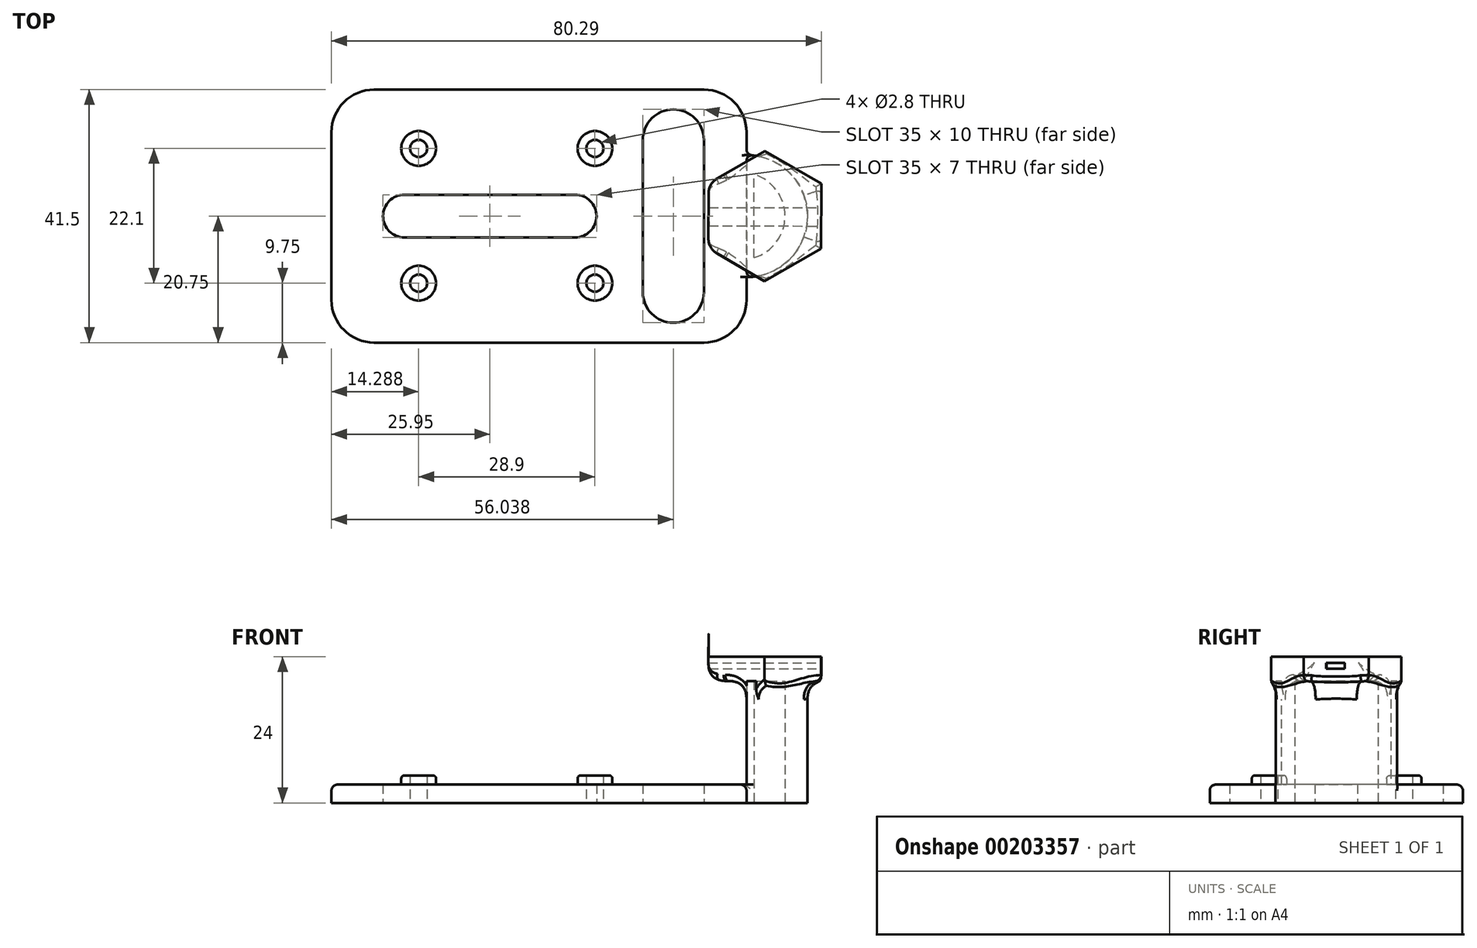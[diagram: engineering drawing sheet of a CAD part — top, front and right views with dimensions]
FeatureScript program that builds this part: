
annotation { "Feature Type Name" : "Feature", "Feature Type Description" : "" }
export const myFeature = defineFeature(function(context is Context, id is Id, definition is map)
    precondition{}
    {
        {
            var Q0;
            Q0=qCreatedBy(makeId("Top.planeOp"),FACE);
            var sketch = newSketch(context, id + "F0", { "sketchPlane" : qUnion([Q0])});
            skLineSegment(sketch, "E0.bottom", {"start": v(42.09, 20.75) * mm, "end": v(-25.95, 20.75) * mm});
            skLineSegment(sketch, "E0.top", {"start": v(42.09, -20.75) * mm, "end": v(-25.95, -20.75) * mm});
            skLineSegment(sketch, "E0.left", {"start": v(42.09, 20.75) * mm, "end": v(42.09, -20.75) * mm});
            skPoint(sketch, "E0.middle", {"position": v(0, 0) * mm});
            skCircle(sketch, "E1", {"center": v(-11.66, 11.1) * mm, "radius": 2.85 * mm});
            skCircle(sketch, "E2", {"center": v(-11.66, -11) * mm, "radius": 2.85 * mm});
            skCircle(sketch, "E3", {"center": v(17.24, 11.1) * mm, "radius": 2.85 * mm});
            skCircle(sketch, "E4", {"center": v(17.24, -11) * mm, "radius": 2.85 * mm});
            skCircle(sketch, "E5", {"center": v(-11.66, 11.1) * mm, "radius": 1.4 * mm});
            skCircle(sketch, "E6", {"center": v(17.24, 11.1) * mm, "radius": 1.4 * mm});
            skCircle(sketch, "E7", {"center": v(-11.66, -11) * mm, "radius": 1.4 * mm});
            skCircle(sketch, "E8", {"center": v(17.24, -11) * mm, "radius": 1.4 * mm});
            skLineSegment(sketch, "E9.left", {"start": v(-25.95, 12.5) * mm, "end": v(-25.95, -12.5) * mm});
            skLineSegment(sketch, "E10.bottom", {"start": v(14, 3.5) * mm, "end": v(-14, 3.5) * mm});
            skLineSegment(sketch, "E10.top", {"start": v(14, -3.5) * mm, "end": v(-14, -3.5) * mm});
            skLineSegment(sketch, "E10.left", {"start": v(17.5, 0) * mm, "end": v(17.5, 0) * mm});
            skLineSegment(sketch, "E10.right", {"start": v(-17.5, 0) * mm, "end": v(-17.5, 0) * mm});
            skLineSegment(sketch, "E11.bottom", {"start": v(30.09, 17.5) * mm, "end": v(30.09, 17.5) * mm});
            skLineSegment(sketch, "E11.top", {"start": v(30.09, -17.5) * mm, "end": v(30.09, -17.5) * mm});
            skLineSegment(sketch, "E11.left", {"start": v(35.09, 12.5) * mm, "end": v(35.09, -12.5) * mm});
            skLineSegment(sketch, "E11.right", {"start": v(25.09, 12.5) * mm, "end": v(25.09, -12.5) * mm});
            skPoint(sketch, "E11.middle", {"position": v(30.09, 0) * mm});
            skPoint(sketch, "E12.visualSharp", {"position": v(-25.95, 17.5) * mm});
            skPoint(sketch, "E13.visualSharp", {"position": v(-25.95, -17.5) * mm});
            skPoint(sketch, "E14.visualSharp", {"position": v(25.09, -17.5) * mm});
            skArc(sketch, "E14.filletArc", {"start": v(25.09, -12.5) * mm, "mid": v(26.55, -16.04) * mm, "end": v(30.09, -17.5) * mm});
            skPoint(sketch, "E15.visualSharp", {"position": v(35.09, -17.5) * mm});
            skArc(sketch, "E15.filletArc", {"start": v(30.09, -17.5) * mm, "mid": v(33.62, -16.04) * mm, "end": v(35.09, -12.5) * mm});
            skPoint(sketch, "E16.visualSharp", {"position": v(35.09, 17.5) * mm});
            skArc(sketch, "E16.filletArc", {"start": v(35.09, 12.5) * mm, "mid": v(33.62, 16.04) * mm, "end": v(30.09, 17.5) * mm});
            skPoint(sketch, "E17.visualSharp", {"position": v(25.09, 17.5) * mm});
            skArc(sketch, "E17.filletArc", {"start": v(30.09, 17.5) * mm, "mid": v(26.55, 16.04) * mm, "end": v(25.09, 12.5) * mm});
            skPoint(sketch, "E18.visualSharp", {"position": v(17.5, 3.5) * mm});
            skArc(sketch, "E18.filletArc", {"start": v(17.5, 0) * mm, "mid": v(16.47, 2.47) * mm, "end": v(14, 3.5) * mm});
            skPoint(sketch, "E19.visualSharp", {"position": v(17.5, -3.5) * mm});
            skArc(sketch, "E19.filletArc", {"start": v(14, -3.5) * mm, "mid": v(16.47, -2.47) * mm, "end": v(17.5, 0) * mm});
            skPoint(sketch, "E20.visualSharp", {"position": v(-17.5, -3.5) * mm});
            skArc(sketch, "E20.filletArc", {"start": v(-17.5, 0) * mm, "mid": v(-16.47, -2.47) * mm, "end": v(-14, -3.5) * mm});
            skPoint(sketch, "E21.visualSharp", {"position": v(-17.5, 3.5) * mm});
            skArc(sketch, "E21.filletArc", {"start": v(-14, 3.5) * mm, "mid": v(-16.47, 2.47) * mm, "end": v(-17.5, 0) * mm});
            skArc(sketch, "E22", {"start": v(42.09, -10) * mm, "mid": v(52.09, 0) * mm, "end": v(42.09, 10) * mm});
            skArc(sketch, "E23", {"start": v(43.34, -6.83) * mm, "mid": v(48.4, 0) * mm, "end": v(43.34, 6.83) * mm});
            skLineSegment(sketch, "E24", {"start": v(43.34, -6.83) * mm, "end": v(43.34, 6.83) * mm});
            skLineSegment(sketch, "E25", {"start": v(-25.95, 20.75) * mm, "end": v(-25.95, -20.75) * mm});
            skSolve(sketch);
        }
        {
            var Q0;
            Q0=makeQuery(id+"F0.imprint","IMPRINT",FACE,{"disambiguationData":[TD([[makeQuery(id+"F0.imprint","IMPRINT",EDGE,{"derivedFrom":sQuery(id+"F0.wireOp",EDGE,"E0.bottom")}),1.0]])]});
            var Q1;
            Q1=makeQuery(id+"F0.imprint","IMPRINT",FACE,{"disambiguationData":[TD([[makeQuery(id+"F0.imprint","IMPRINT",EDGE,{"derivedFrom":sQuery(id+"F0.wireOp",EDGE,"E3")}),1.0]])]});
            var Q2;
            Q2=makeQuery(id+"F0.imprint","IMPRINT",FACE,{"disambiguationData":[TD([[makeQuery(id+"F0.imprint","IMPRINT",EDGE,{"derivedFrom":sQuery(id+"F0.wireOp",EDGE,"E1")}),1.0]])]});
            var Q3;
            Q3=makeQuery(id+"F0.imprint","IMPRINT",FACE,{"disambiguationData":[TD([[makeQuery(id+"F0.imprint","IMPRINT",EDGE,{"derivedFrom":sQuery(id+"F0.wireOp",EDGE,"E2")}),1.0]])]});
            var Q4;
            Q4=makeQuery(id+"F0.imprint","IMPRINT",FACE,{"disambiguationData":[TD([[makeQuery(id+"F0.imprint","IMPRINT",EDGE,{"derivedFrom":sQuery(id+"F0.wireOp",EDGE,"E4")}),1.0]])]});
            extrude(context, id + "F1", {"entities" : qUnion([Q0, Q1, Q2, Q3, Q4]), "depth" : 3 * mm});
        }
        {
            var Q0;
            Q0=makeQuery(id+"F0.imprint","IMPRINT",FACE,{"disambiguationData":[TD([[makeQuery(id+"F0.imprint","IMPRINT",EDGE,{"derivedFrom":sQuery(id+"F0.wireOp",EDGE,"E1")}),1.0]])]});
            var Q1;
            Q1=makeQuery(id+"F0.imprint","IMPRINT",FACE,{"disambiguationData":[TD([[makeQuery(id+"F0.imprint","IMPRINT",EDGE,{"derivedFrom":sQuery(id+"F0.wireOp",EDGE,"E2")}),1.0]])]});
            var Q2;
            Q2=makeQuery(id+"F0.imprint","IMPRINT",FACE,{"disambiguationData":[TD([[makeQuery(id+"F0.imprint","IMPRINT",EDGE,{"derivedFrom":sQuery(id+"F0.wireOp",EDGE,"E4")}),1.0]])]});
            var Q3;
            Q3=makeQuery(id+"F0.imprint","IMPRINT",FACE,{"disambiguationData":[TD([[makeQuery(id+"F0.imprint","IMPRINT",EDGE,{"derivedFrom":sQuery(id+"F0.wireOp",EDGE,"E3")}),1.0]])]});
            extrude(context, id + "F2", {"entities" : qUnion([Q0, Q1, Q2, Q3]), "operationType" : NewBodyOperationType.ADD, "depth" : 4.5 * mm});
        }
        {
            var Q0;
            Q0=makeQuery(id+"F1.opExtrude","SWEPT_EDGE",EDGE,{"disambiguationData":[OSD([sQuery(id+"F0.wireOp",EDGE,"E0.top"),sQuery(id+"F0.wireOp",EDGE,"E0.right")])]});
            var Q1;
            Q1=makeQuery(id+"F1.opExtrude","SWEPT_EDGE",EDGE,{"disambiguationData":[OSD([sQuery(id+"F0.wireOp",EDGE,"E0.bottom"),sQuery(id+"F0.wireOp",EDGE,"E0.right")])]});
            var Q2;
            Q2=makeQuery(id+"F1.opExtrude","SWEPT_EDGE",EDGE,{"disambiguationData":[OSD([sQuery(id+"F0.wireOp",EDGE,"E0.top"),sQuery(id+"F0.wireOp",EDGE,"E0.left")])]});
            var Q3;
            Q3=makeQuery(id+"F1.opExtrude","SWEPT_EDGE",EDGE,{"disambiguationData":[OSD([sQuery(id+"F0.wireOp",EDGE,"E0.bottom"),sQuery(id+"F0.wireOp",EDGE,"E0.left")])]});
            fillet(context, id + "F3", {"entities" : qUnion([Q0, Q1, Q2, Q3]), "radius" : 7 * mm, "tangentPropagation" : true, "allowEdgeOverflow" : false});
        }
        {
            var Q0;
            Q0=makeQuery(id+"F2.opExtrude","CAP_EDGE",EDGE,{"disambiguationData":[OSD([sQuery(id+"F0.wireOp",EDGE,"E3")])],"isStart":false});
            var Q1;
            Q1=makeQuery(id+"F2.opExtrude","CAP_EDGE",EDGE,{"disambiguationData":[OSD([sQuery(id+"F0.wireOp",EDGE,"E1")])],"isStart":false});
            var Q2;
            Q2=makeQuery(id+"F2.opExtrude","CAP_EDGE",EDGE,{"disambiguationData":[OSD([sQuery(id+"F0.wireOp",EDGE,"E2")])],"isStart":false});
            var Q3;
            Q3=makeQuery(id+"F2.opExtrude","CAP_EDGE",EDGE,{"disambiguationData":[OSD([sQuery(id+"F0.wireOp",EDGE,"E4")])],"isStart":false});
            fillet(context, id + "F4", {"entities" : qUnion([Q0, Q1, Q2, Q3]), "radius" : 0.5 * mm, "tangentPropagation" : true, "allowEdgeOverflow" : false});
        }
        {
            var Q0;
            {var subQ0=sQuery(id+"F0.wireOp",EDGE,"E22");Q0=makeQuery(id+"F0.imprint","IMPRINT",FACE,{"disambiguationData":[TD([[makeQuery(id+"F0.imprint","IMPRINT",EDGE,{"derivedFrom":subQ0}),1.0]])]});}
            extrude(context, id + "F5", {"entities" : qUnion([Q0]), "operationType" : NewBodyOperationType.ADD, "depth" : 20 * mm});
        }
        {
            var Q0;
            Q0=makeQuery(id+"F5.opExtrude","CAP_FACE",FACE,{"disambiguationData":[OSD([sQuery(id+"F0.wireOp",EDGE,"E0.left"),sQuery(id+"F0.wireOp",EDGE,"E22"),sQuery(id+"F0.wireOp",EDGE,"E23"),sQuery(id+"F0.wireOp",EDGE,"E24")])],"isStart":false});
            var sketch = newSketch(context, id + "F6", { "sketchPlane" : qUnion([Q0])});
            skCircle(sketch, "E26.cCircle", {"center": v(45.08, 0) * mm, "radius": 9.24 * mm, "construction": true});
            skLineSegment(sketch, "E26.0", {"start": v(45.11, 10.67) * mm, "end": v(54.34, 5.31) * mm});
            skLineSegment(sketch, "E26.1", {"start": v(54.34, 5.31) * mm, "end": v(54.3, -5.36) * mm});
            skLineSegment(sketch, "E26.2", {"start": v(54.3, -5.36) * mm, "end": v(45.05, -10.67) * mm});
            skLineSegment(sketch, "E26.3", {"start": v(45.05, -10.67) * mm, "end": v(35.83, -5.31) * mm});
            skLineSegment(sketch, "E26.4", {"start": v(35.83, -5.31) * mm, "end": v(35.86, 5.36) * mm});
            skLineSegment(sketch, "E26.5", {"start": v(35.86, 5.36) * mm, "end": v(45.11, 10.67) * mm});
            skPoint(sketch, "E26.0.midPoint", {"position": v(49.72, 7.99) * mm});
            skSolve(sketch);
        }
        {
            var Q0;
            Q0 = qSketchRegion(id + "F6", true);
            extrude(context, id + "F7", {"entities" : qUnion([Q0]), "operationType" : NewBodyOperationType.ADD, "depth" : 4 * mm});
        }
        {
            var Q0;
            {var subQ0=sQuery(id+"F0.wireOp",EDGE,"E0.left");var subQ1=sQuery(id+"F0.wireOp",EDGE,"E22");Q0=makeQuery(id+"F5.boolean.opBoolean","SPLIT",EDGE,{"disambiguationData":[topologyDisambiguationEdgeConnected([makeQuery(id+"F5.opExtrude","SWEPT_FACE",FACE,{"disambiguationData":[OSD([subQ0])]})])],"derivedFrom":makeQuery(id+"F5.opExtrude","SWEPT_EDGE",EDGE,{"disambiguationData":[OSD([subQ0,subQ1]),TDD([makeQuery(id+"F0.imprint","INTERSECT",VERTEX,{"disambiguationData":[OD(0.0)],"derivedFrom":[subQ0,subQ1]})])]})});}
            var Q1;
            {var subQ0=sQuery(id+"F0.wireOp",EDGE,"E0.left");var subQ1=sQuery(id+"F0.wireOp",EDGE,"E22");Q1=makeQuery(id+"F5.boolean.opBoolean","SPLIT",EDGE,{"disambiguationData":[topologyDisambiguationEdgeConnected([makeQuery(id+"F5.opExtrude","SWEPT_FACE",FACE,{"disambiguationData":[OSD([subQ0])]})])],"derivedFrom":makeQuery(id+"F5.opExtrude","SWEPT_EDGE",EDGE,{"disambiguationData":[OSD([subQ0,subQ1]),TDD([makeQuery(id+"F0.imprint","INTERSECT",VERTEX,{"disambiguationData":[OD(1.0)],"derivedFrom":[subQ0,subQ1]})])]})});}
            fillet(context, id + "F8", {"entities" : qUnion([Q0, Q1]), "radius" : 1 * mm, "tangentPropagation" : true, "rho" : 0.5, "crossSection" : FilletCrossSection.CONIC, "allowEdgeOverflow" : false});
        }
        {
            var Q0;
            {var subQ0=sQuery(id+"F0.wireOp",EDGE,"E0.left");var subQ1=sQuery(id+"F0.wireOp",EDGE,"E22");Q0=makeQuery(id+"F5.boolean.opBoolean","SPLIT",EDGE,{"disambiguationData":[topologyDisambiguationEdgeConnected([makeQuery(id+"F1.opExtrude","SWEPT_FACE",FACE,{"disambiguationData":[OSD([subQ0])]})])],"derivedFrom":makeQuery(id+"F5.opExtrude","SWEPT_EDGE",EDGE,{"disambiguationData":[OSD([subQ0,subQ1]),TDD([makeQuery(id+"F0.imprint","INTERSECT",VERTEX,{"disambiguationData":[OD(1.0)],"derivedFrom":[subQ0,subQ1]})])]})});}
            var Q1;
            {var subQ0=sQuery(id+"F0.wireOp",EDGE,"E0.left");var subQ1=sQuery(id+"F0.wireOp",EDGE,"E22");Q1=makeQuery(id+"F5.boolean.opBoolean","SPLIT",EDGE,{"disambiguationData":[topologyDisambiguationEdgeConnected([makeQuery(id+"F1.opExtrude","SWEPT_FACE",FACE,{"disambiguationData":[OSD([subQ0])]})])],"derivedFrom":makeQuery(id+"F5.opExtrude","SWEPT_EDGE",EDGE,{"disambiguationData":[OSD([subQ0,subQ1]),TDD([makeQuery(id+"F0.imprint","INTERSECT",VERTEX,{"disambiguationData":[OD(0.0)],"derivedFrom":[subQ0,subQ1]})])]})});}
            fillet(context, id + "F9", {"entities" : qUnion([Q0, Q1]), "radius" : 1 * mm, "tangentPropagation" : true, "allowEdgeOverflow" : false});
        }
        {
            var Q0;
            {var subQ0=sQuery(id+"F0.wireOp",EDGE,"E0.left");Q0=makeQuery(id+"F7.boolean.opBoolean","SPLIT",EDGE,{"disambiguationData":[topologyDisambiguationEdgeConnected([makeQuery(id+"F5.opExtrude","SWEPT_FACE",FACE,{"disambiguationData":[OSD([subQ0])]}),makeQuery(id+"F7.opExtrude","CAP_FACE",FACE,{"disambiguationData":[OSD([sQuery(id+"F6.wireOp",EDGE,"E26.0"),sQuery(id+"F6.wireOp",EDGE,"E26.1"),sQuery(id+"F6.wireOp",EDGE,"E26.2"),sQuery(id+"F6.wireOp",EDGE,"E26.3"),sQuery(id+"F6.wireOp",EDGE,"E26.4"),sQuery(id+"F6.wireOp",EDGE,"E26.5")])],"isStart":true})])],"derivedFrom":makeQuery(id+"F5.opExtrude","CAP_EDGE",EDGE,{"disambiguationData":[OSD([subQ0])],"isStart":false})});}
            var Q1;
            Q1=makeQuery(id+"F7.opExtrude","CAP_EDGE",EDGE,{"disambiguationData":[OSD([sQuery(id+"F6.wireOp",EDGE,"E26.4")])],"isStart":true});
            var Q2;
            {var subQ0=sQuery(id+"F0.wireOp",EDGE,"E22");Q2=makeQuery(id+"F7.boolean.opBoolean","SPLIT",EDGE,{"disambiguationData":[topologyDisambiguationEdgeConnected([makeQuery(id+"F5.opExtrude","SWEPT_FACE",FACE,{"disambiguationData":[OSD([subQ0])]}),makeQuery(id+"F7.opExtrude","CAP_FACE",FACE,{"disambiguationData":[OSD([sQuery(id+"F6.wireOp",EDGE,"E26.0"),sQuery(id+"F6.wireOp",EDGE,"E26.1"),sQuery(id+"F6.wireOp",EDGE,"E26.2"),sQuery(id+"F6.wireOp",EDGE,"E26.3"),sQuery(id+"F6.wireOp",EDGE,"E26.4"),sQuery(id+"F6.wireOp",EDGE,"E26.5")])],"isStart":true})])],"derivedFrom":makeQuery(id+"F5.opExtrude","CAP_EDGE",EDGE,{"disambiguationData":[OSD([subQ0])],"isStart":false})});}
            var Q3;
            Q3=makeQuery(id+"F7.opExtrude","SWEPT_EDGE",EDGE,{"disambiguationData":[OSD([sQuery(id+"F6.wireOp",EDGE,"E26.3"),sQuery(id+"F6.wireOp",EDGE,"E26.4")])]});
            var Q4;
            Q4=makeQuery(id+"F7.opExtrude","SWEPT_EDGE",EDGE,{"disambiguationData":[OSD([sQuery(id+"F6.wireOp",EDGE,"E26.4"),sQuery(id+"F6.wireOp",EDGE,"E26.5")])]});
            fillet(context, id + "F10", {"entities" : qUnion([Q0, Q1, Q2, Q3, Q4]), "radius" : 3 * mm, "tangentPropagation" : true, "rho" : 0.5, "crossSection" : FilletCrossSection.CONIC, "allowEdgeOverflow" : false});
        }
        {
            var Q0;
            {var subQ0=sQuery(id+"F0.wireOp",EDGE,"E0.left");Q0=makeQuery(id+"F5.boolean.opBoolean","SPLIT",EDGE,{"disambiguationData":[topologyDisambiguationEdgeConnected([makeQuery(id+"F1.opExtrude","CAP_FACE",FACE,{"disambiguationData":[OSD([sQuery(id+"F0.wireOp",EDGE,"E0.bottom"),sQuery(id+"F0.wireOp",EDGE,"E0.top"),subQ0,sQuery(id+"F0.wireOp",EDGE,"E5"),sQuery(id+"F0.wireOp",EDGE,"E6"),sQuery(id+"F0.wireOp",EDGE,"E7"),sQuery(id+"F0.wireOp",EDGE,"E8"),sQuery(id+"F0.wireOp",EDGE,"E10.bottom"),sQuery(id+"F0.wireOp",EDGE,"E10.top"),sQuery(id+"F0.wireOp",EDGE,"E11.left"),sQuery(id+"F0.wireOp",EDGE,"E11.right"),sQuery(id+"F0.wireOp",EDGE,"E14.filletArc"),sQuery(id+"F0.wireOp",EDGE,"E15.filletArc"),sQuery(id+"F0.wireOp",EDGE,"E16.filletArc"),sQuery(id+"F0.wireOp",EDGE,"E17.filletArc"),sQuery(id+"F0.wireOp",EDGE,"E18.filletArc"),sQuery(id+"F0.wireOp",EDGE,"E19.filletArc"),sQuery(id+"F0.wireOp",EDGE,"E20.filletArc"),sQuery(id+"F0.wireOp",EDGE,"E21.filletArc"),sQuery(id+"F0.wireOp",EDGE,"E25")])],"isStart":false}),makeQuery(id+"F5.opExtrude","SWEPT_FACE",FACE,{"disambiguationData":[OSD([subQ0])]})])],"derivedFrom":makeQuery(id+"F1.opExtrude","CAP_EDGE",EDGE,{"disambiguationData":[OSD([subQ0])],"isStart":false})});}
            var Q1;
            {var subQ0=sQuery(id+"F6.wireOp",EDGE,"E26.3");var subQ1=sQuery(id+"F0.wireOp",EDGE,"E0.left");Q1=makeQuery(id+"F10.opFillet","BLEND_EDGE",EDGE,{"blendedFrom":[makeQuery(id+"F7.boolean.opBoolean","SPLIT",EDGE,{"disambiguationData":[topologyDisambiguationEdgeConnected([makeQuery(id+"F5.opExtrude","SWEPT_FACE",FACE,{"disambiguationData":[OSD([subQ1])]}),makeQuery(id+"F7.opExtrude","CAP_FACE",FACE,{"disambiguationData":[OSD([sQuery(id+"F6.wireOp",EDGE,"E26.0"),sQuery(id+"F6.wireOp",EDGE,"E26.1"),sQuery(id+"F6.wireOp",EDGE,"E26.2"),subQ0,sQuery(id+"F6.wireOp",EDGE,"E26.4"),sQuery(id+"F6.wireOp",EDGE,"E26.5")])],"isStart":true})])],"derivedFrom":makeQuery(id+"F5.opExtrude","CAP_EDGE",EDGE,{"disambiguationData":[OSD([subQ1])],"isStart":false})}),makeQuery(id+"F7.opExtrude","SWEPT_FACE",FACE,{"disambiguationData":[OSD([subQ0])]})],"blendedInto":[makeQuery(id+"F7.opExtrude","SWEPT_FACE",FACE,{"disambiguationData":[OSD([subQ0])]})]});}
            var Q2;
            {var subQ0=sQuery(id+"F6.wireOp",EDGE,"E26.3");var subQ1=sQuery(id+"F0.wireOp",EDGE,"E22");Q2=makeQuery(id+"F10.opFillet","BLEND_EDGE",EDGE,{"blendedFrom":[makeQuery(id+"F7.boolean.opBoolean","SPLIT",EDGE,{"disambiguationData":[topologyDisambiguationEdgeConnected([makeQuery(id+"F5.opExtrude","SWEPT_FACE",FACE,{"disambiguationData":[OSD([subQ1])]}),makeQuery(id+"F7.opExtrude","CAP_FACE",FACE,{"disambiguationData":[OSD([sQuery(id+"F6.wireOp",EDGE,"E26.0"),sQuery(id+"F6.wireOp",EDGE,"E26.1"),sQuery(id+"F6.wireOp",EDGE,"E26.2"),subQ0,sQuery(id+"F6.wireOp",EDGE,"E26.4"),sQuery(id+"F6.wireOp",EDGE,"E26.5")])],"isStart":true})])],"derivedFrom":makeQuery(id+"F5.opExtrude","CAP_EDGE",EDGE,{"disambiguationData":[OSD([subQ1])],"isStart":false})}),makeQuery(id+"F7.opExtrude","SWEPT_FACE",FACE,{"disambiguationData":[OSD([subQ0])]})],"blendedInto":[makeQuery(id+"F7.opExtrude","SWEPT_FACE",FACE,{"disambiguationData":[OSD([subQ0])]})]});}
            var Q3;
            {var subQ0=sQuery(id+"F6.wireOp",EDGE,"E26.2");var subQ1=sQuery(id+"F0.wireOp",EDGE,"E22");Q3=makeQuery(id+"F10.opFillet","BLEND_EDGE",EDGE,{"blendedFrom":[makeQuery(id+"F7.boolean.opBoolean","SPLIT",EDGE,{"disambiguationData":[topologyDisambiguationEdgeConnected([makeQuery(id+"F5.opExtrude","SWEPT_FACE",FACE,{"disambiguationData":[OSD([subQ1])]}),makeQuery(id+"F7.opExtrude","CAP_FACE",FACE,{"disambiguationData":[OSD([sQuery(id+"F6.wireOp",EDGE,"E26.0"),sQuery(id+"F6.wireOp",EDGE,"E26.1"),subQ0,sQuery(id+"F6.wireOp",EDGE,"E26.3"),sQuery(id+"F6.wireOp",EDGE,"E26.4"),sQuery(id+"F6.wireOp",EDGE,"E26.5")])],"isStart":true})])],"derivedFrom":makeQuery(id+"F5.opExtrude","CAP_EDGE",EDGE,{"disambiguationData":[OSD([subQ1])],"isStart":false})}),makeQuery(id+"F7.opExtrude","SWEPT_FACE",FACE,{"disambiguationData":[OSD([subQ0])]})],"blendedInto":[makeQuery(id+"F7.opExtrude","SWEPT_FACE",FACE,{"disambiguationData":[OSD([subQ0])]})]});}
            var Q4;
            {var subQ0=sQuery(id+"F6.wireOp",EDGE,"E26.1");var subQ1=sQuery(id+"F0.wireOp",EDGE,"E22");Q4=makeQuery(id+"F10.opFillet","BLEND_EDGE",EDGE,{"blendedFrom":[makeQuery(id+"F7.boolean.opBoolean","SPLIT",EDGE,{"disambiguationData":[topologyDisambiguationEdgeConnected([makeQuery(id+"F5.opExtrude","SWEPT_FACE",FACE,{"disambiguationData":[OSD([subQ1])]}),makeQuery(id+"F7.opExtrude","CAP_FACE",FACE,{"disambiguationData":[OSD([sQuery(id+"F6.wireOp",EDGE,"E26.0"),subQ0,sQuery(id+"F6.wireOp",EDGE,"E26.2"),sQuery(id+"F6.wireOp",EDGE,"E26.3"),sQuery(id+"F6.wireOp",EDGE,"E26.4"),sQuery(id+"F6.wireOp",EDGE,"E26.5")])],"isStart":true})])],"derivedFrom":makeQuery(id+"F5.opExtrude","CAP_EDGE",EDGE,{"disambiguationData":[OSD([subQ1])],"isStart":false})}),makeQuery(id+"F7.opExtrude","SWEPT_FACE",FACE,{"disambiguationData":[OSD([subQ0])]})],"blendedInto":[makeQuery(id+"F7.opExtrude","SWEPT_FACE",FACE,{"disambiguationData":[OSD([subQ0])]})]});}
            var Q5;
            {var subQ0=sQuery(id+"F6.wireOp",EDGE,"E26.0");var subQ1=sQuery(id+"F0.wireOp",EDGE,"E22");Q5=makeQuery(id+"F10.opFillet","BLEND_EDGE",EDGE,{"blendedFrom":[makeQuery(id+"F7.boolean.opBoolean","SPLIT",EDGE,{"disambiguationData":[topologyDisambiguationEdgeConnected([makeQuery(id+"F5.opExtrude","SWEPT_FACE",FACE,{"disambiguationData":[OSD([subQ1])]}),makeQuery(id+"F7.opExtrude","CAP_FACE",FACE,{"disambiguationData":[OSD([subQ0,sQuery(id+"F6.wireOp",EDGE,"E26.1"),sQuery(id+"F6.wireOp",EDGE,"E26.2"),sQuery(id+"F6.wireOp",EDGE,"E26.3"),sQuery(id+"F6.wireOp",EDGE,"E26.4"),sQuery(id+"F6.wireOp",EDGE,"E26.5")])],"isStart":true})])],"derivedFrom":makeQuery(id+"F5.opExtrude","CAP_EDGE",EDGE,{"disambiguationData":[OSD([subQ1])],"isStart":false})}),makeQuery(id+"F7.opExtrude","SWEPT_FACE",FACE,{"disambiguationData":[OSD([subQ0])]})],"blendedInto":[makeQuery(id+"F7.opExtrude","SWEPT_FACE",FACE,{"disambiguationData":[OSD([subQ0])]})]});}
            var Q6;
            {var subQ0=sQuery(id+"F6.wireOp",EDGE,"E26.5");var subQ1=sQuery(id+"F0.wireOp",EDGE,"E22");Q6=makeQuery(id+"F10.opFillet","BLEND_EDGE",EDGE,{"blendedFrom":[makeQuery(id+"F7.boolean.opBoolean","SPLIT",EDGE,{"disambiguationData":[topologyDisambiguationEdgeConnected([makeQuery(id+"F5.opExtrude","SWEPT_FACE",FACE,{"disambiguationData":[OSD([subQ1])]}),makeQuery(id+"F7.opExtrude","CAP_FACE",FACE,{"disambiguationData":[OSD([sQuery(id+"F6.wireOp",EDGE,"E26.0"),sQuery(id+"F6.wireOp",EDGE,"E26.1"),sQuery(id+"F6.wireOp",EDGE,"E26.2"),sQuery(id+"F6.wireOp",EDGE,"E26.3"),sQuery(id+"F6.wireOp",EDGE,"E26.4"),subQ0])],"isStart":true})])],"derivedFrom":makeQuery(id+"F5.opExtrude","CAP_EDGE",EDGE,{"disambiguationData":[OSD([subQ1])],"isStart":false})}),makeQuery(id+"F7.opExtrude","SWEPT_FACE",FACE,{"disambiguationData":[OSD([subQ0])]})],"blendedInto":[makeQuery(id+"F7.opExtrude","SWEPT_FACE",FACE,{"disambiguationData":[OSD([subQ0])]})]});}
            var Q7;
            {var subQ0=sQuery(id+"F6.wireOp",EDGE,"E26.5");var subQ1=sQuery(id+"F0.wireOp",EDGE,"E0.left");Q7=makeQuery(id+"F10.opFillet","BLEND_EDGE",EDGE,{"blendedFrom":[makeQuery(id+"F7.boolean.opBoolean","SPLIT",EDGE,{"disambiguationData":[topologyDisambiguationEdgeConnected([makeQuery(id+"F5.opExtrude","SWEPT_FACE",FACE,{"disambiguationData":[OSD([subQ1])]}),makeQuery(id+"F7.opExtrude","CAP_FACE",FACE,{"disambiguationData":[OSD([sQuery(id+"F6.wireOp",EDGE,"E26.0"),sQuery(id+"F6.wireOp",EDGE,"E26.1"),sQuery(id+"F6.wireOp",EDGE,"E26.2"),sQuery(id+"F6.wireOp",EDGE,"E26.3"),sQuery(id+"F6.wireOp",EDGE,"E26.4"),subQ0])],"isStart":true})])],"derivedFrom":makeQuery(id+"F5.opExtrude","CAP_EDGE",EDGE,{"disambiguationData":[OSD([subQ1])],"isStart":false})}),makeQuery(id+"F7.opExtrude","SWEPT_FACE",FACE,{"disambiguationData":[OSD([subQ0])]})],"blendedInto":[makeQuery(id+"F7.opExtrude","SWEPT_FACE",FACE,{"disambiguationData":[OSD([subQ0])]})]});}
            fillet(context, id + "F11", {"entities" : qUnion([Q0, Q1, Q2, Q3, Q4, Q5, Q6, Q7]), "radius" : 1 * mm, "tangentPropagation" : true, "allowEdgeOverflow" : false});
        }
        {
            var Q0;
            Q0=makeQuery(id+"F7.opExtrude","SWEPT_FACE",FACE,{"disambiguationData":[OSD([sQuery(id+"F6.wireOp",EDGE,"E26.1")])]});
            var sketch = newSketch(context, id + "F12", { "sketchPlane" : qUnion([Q0])});
            skLineSegment(sketch, "E27.bottom", {"start": v(1.5, 23) * mm, "end": v(-1.5, 23) * mm});
            skLineSegment(sketch, "E27.top", {"start": v(1.5, 22) * mm, "end": v(-1.5, 22) * mm});
            skLineSegment(sketch, "E27.left", {"start": v(1.5, 23) * mm, "end": v(1.5, 22) * mm});
            skLineSegment(sketch, "E27.right", {"start": v(-1.5, 23) * mm, "end": v(-1.5, 22) * mm});
            skPoint(sketch, "E27.middle", {"position": v(0, 22.5) * mm});
            skPoint(sketch, "E27.middle.positionSnap0", {"position": v(-5.22, 22.5) * mm});
            skPoint(sketch, "E27.centerSnap0", {"position": v(-5.22, 22.5) * mm});
            skSolve(sketch);
        }
        {
            var Q0;
            Q0 = qSketchRegion(id + "F12", true);
            extrude(context, id + "F13", {"entities" : qUnion([Q0]), "operationType" : NewBodyOperationType.REMOVE, "oppositeDirection" : true, "depth" : 25 * mm, "hasSecondDirection" : true, "secondDirectionOppositeDirection" : false, "secondDirectionDepth" : 25 * mm});
        }
    });
